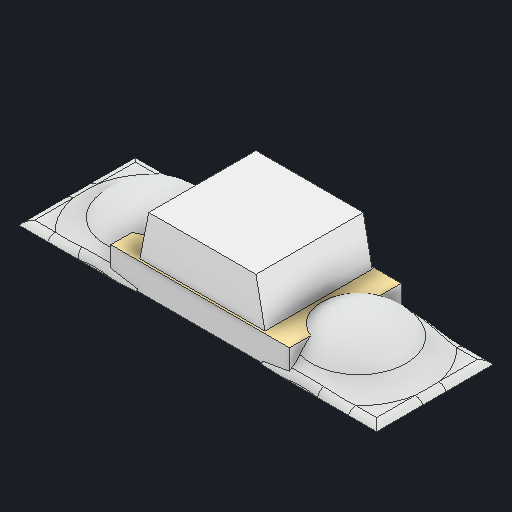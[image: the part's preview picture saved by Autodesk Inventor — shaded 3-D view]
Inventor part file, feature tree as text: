
AUTODESK INVENTOR PART (.ipt)
format: ipt  version: 2023 (Build 270158000, 158)  size: 210,944 bytes
history: native  units: in
note: dims shown in document units (in); Inventor stores cm internally (conversion verified against a paired STEP export)
features: mirror x1, other x1
ambient origin geometry x8: Origin, YZ Plane, XZ Plane, XY Plane, X Axis, Y Axis, Z Axis, Center Point
bodies: Solid1 (feature_tree), Solid2 (feature_tree)
feature tree (2):
  mirror  "Mirror3"
  other  "Boss-Extrude5"
